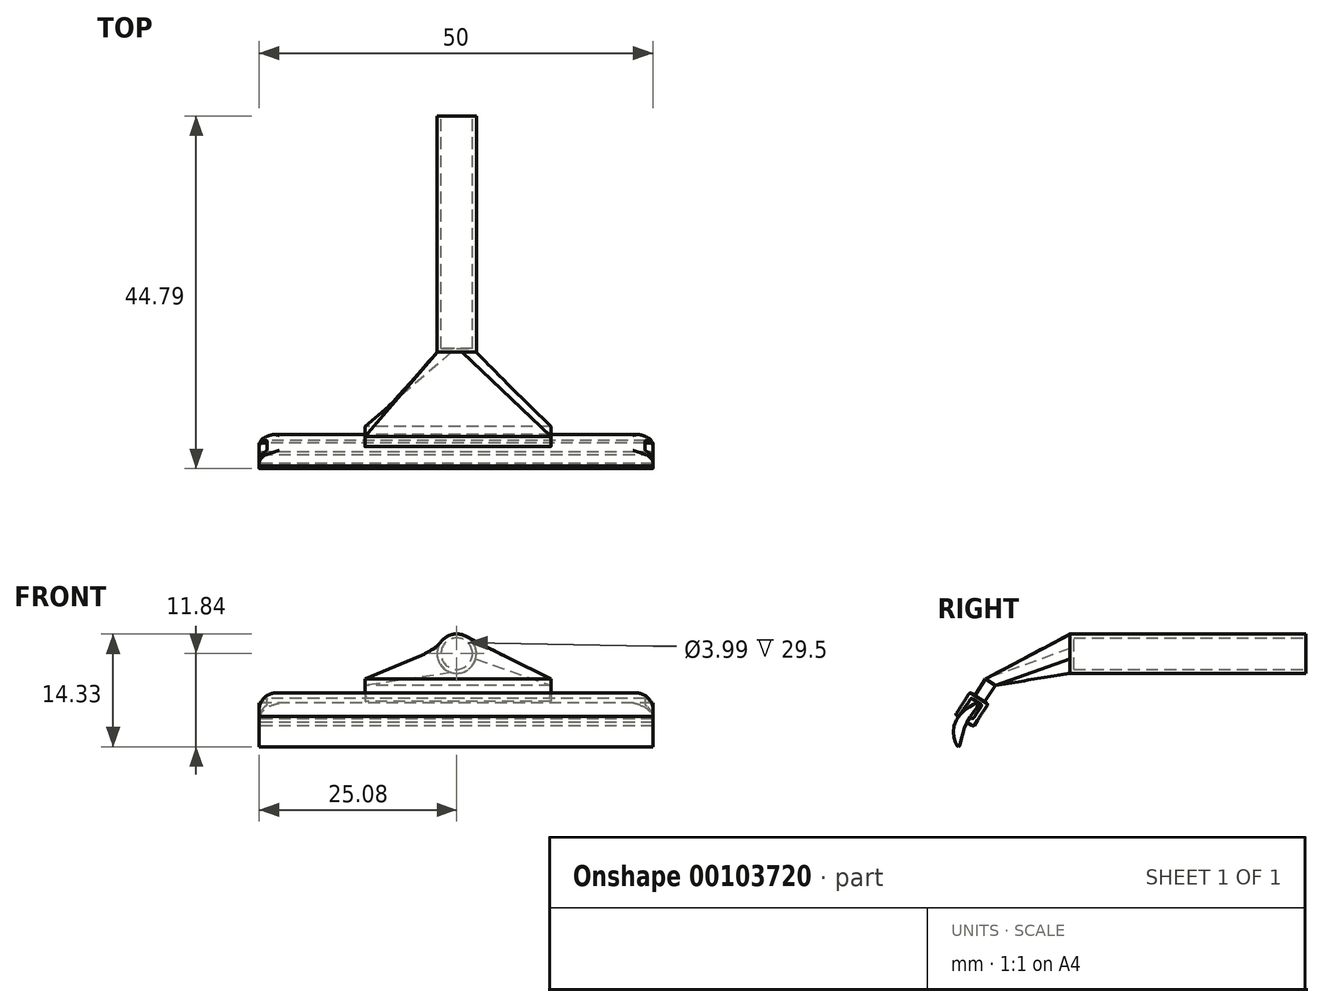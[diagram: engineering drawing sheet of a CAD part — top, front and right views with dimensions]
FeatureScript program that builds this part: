
annotation { "Feature Type Name" : "Feature", "Feature Type Description" : "" }
export const myFeature = defineFeature(function(context is Context, id is Id, definition is map)
    precondition{}
    {
        {
            var Q0;
            Q0=qCreatedBy(makeId("Right.planeOp"),FACE);
            var sketch = newSketch(context, id + "F10", { "sketchPlane" : qUnion([Q0])});
            skFitSpline(sketch, "E0", {"points": [v(-44.18, -11.84) * mm, v(-43.23, -9.04) * mm, v(-41.58, -6.28) * mm, v(-44.56, -8.68) * mm, v(-44.18, -11.84) * mm]});
            skSolve(sketch);
        }
        {
            var Q0;
            Q0=makeQuery(id+"F10.imprint","IMPRINT",FACE,{"disambiguationData":[TD([[makeQuery(id+"F10.imprint","IMPRINT",EDGE,{"derivedFrom":sQuery(id+"F10.wireOp",EDGE,"E0")}),1.0]])]});
            extrude(context, id + "F0", {"entities" : qUnion([Q0]), "depth" : 50 * mm});
        }
        {
            var Q0;
            Q0=qCreatedBy(makeId("Right.planeOp"),FACE);
            var sketch = newSketch(context, id + "F1", { "sketchPlane" : qUnion([Q0])});
            skLineSegment(sketch, "E1", {"start": v(-44.16, -8) * mm, "end": v(-44.39, -7.85) * mm});
            skLineSegment(sketch, "E2", {"start": v(-44.44, -7.6) * mm, "end": v(-42.82, -5.11) * mm});
            skLineSegment(sketch, "E3", {"start": v(-42.48, -5.04) * mm, "end": v(-40.55, -6.3) * mm});
            skLineSegment(sketch, "E4", {"start": v(-40.5, -6.57) * mm, "end": v(-42.15, -9.1) * mm});
            skLineSegment(sketch, "E5", {"start": v(-42.42, -9.15) * mm, "end": v(-43.07, -8.72) * mm});
            skLineSegment(sketch, "E6", {"start": v(-43.07, -8.72) * mm, "end": v(-42.68, -8.1) * mm});
            skLineSegment(sketch, "E7", {"start": v(-42.68, -8.1) * mm, "end": v(-42.48, -8.23) * mm});
            skLineSegment(sketch, "E8", {"start": v(-42.22, -8.18) * mm, "end": v(-41.25, -6.69) * mm});
            skLineSegment(sketch, "E9", {"start": v(-41.3, -6.43) * mm, "end": v(-42.36, -5.73) * mm});
            skLineSegment(sketch, "E10", {"start": v(-42.62, -5.78) * mm, "end": v(-44.16, -8) * mm});
            skPoint(sketch, "E11.visualSharp", {"position": v(-42.69, -4.9) * mm});
            skArc(sketch, "E11.filletArc", {"start": v(-42.48, -5.04) * mm, "mid": v(-42.67, -5) * mm, "end": v(-42.82, -5.11) * mm});
            skPoint(sketch, "E12.visualSharp", {"position": v(-40.4, -6.4) * mm});
            skArc(sketch, "E12.filletArc", {"start": v(-40.5, -6.57) * mm, "mid": v(-40.47, -6.42) * mm, "end": v(-40.55, -6.3) * mm});
            skPoint(sketch, "E13.visualSharp", {"position": v(-42.26, -9.25) * mm});
            skArc(sketch, "E13.filletArc", {"start": v(-42.42, -9.15) * mm, "mid": v(-42.27, -9.18) * mm, "end": v(-42.15, -9.1) * mm});
            skPoint(sketch, "E14.visualSharp", {"position": v(-42.33, -8.34) * mm});
            skArc(sketch, "E14.filletArc", {"start": v(-42.48, -8.23) * mm, "mid": v(-42.34, -8.26) * mm, "end": v(-42.22, -8.18) * mm});
            skPoint(sketch, "E15.visualSharp", {"position": v(-41.14, -6.53) * mm});
            skArc(sketch, "E15.filletArc", {"start": v(-41.25, -6.69) * mm, "mid": v(-41.22, -6.55) * mm, "end": v(-41.3, -6.43) * mm});
            skPoint(sketch, "E16.visualSharp", {"position": v(-42.52, -5.63) * mm});
            skArc(sketch, "E16.filletArc", {"start": v(-42.36, -5.73) * mm, "mid": v(-42.5, -5.7) * mm, "end": v(-42.62, -5.78) * mm});
            skPoint(sketch, "E17.visualSharp", {"position": v(-44.55, -7.75) * mm});
            skArc(sketch, "E17.filletArc", {"start": v(-44.44, -7.6) * mm, "mid": v(-44.47, -7.73) * mm, "end": v(-44.39, -7.85) * mm});
            skSolve(sketch);
        }
        {
            var Q0;
            Q0=makeQuery(id+"F1.imprint","IMPRINT",FACE,{"disambiguationData":[TD([[makeQuery(id+"F1.imprint","IMPRINT",EDGE,{"derivedFrom":sQuery(id+"F1.wireOp",EDGE,"E1")}),-1.0]])]});
            extrude(context, id + "F11", {"entities" : qUnion([Q0]), "depth" : 50 * mm});
        }
        {
            var Q0;
            Q0=makeQuery(id+"F11.opExtrude","SWEPT_FACE",FACE,{"disambiguationData":[OSD([sQuery(id+"F1.wireOp",EDGE,"E3")])]});
            var sketch = newSketch(context, id + "F2", { "sketchPlane" : qUnion([Q0])});
            skLineSegment(sketch, "E18.bottom", {"start": v(37.03, -32.29) * mm, "end": v(13.42, -32.29) * mm});
            skLineSegment(sketch, "E18.top", {"start": v(37.03, -30.78) * mm, "end": v(13.42, -30.78) * mm});
            skLineSegment(sketch, "E18.left", {"start": v(37.03, -32.29) * mm, "end": v(37.03, -30.78) * mm});
            skLineSegment(sketch, "E18.right", {"start": v(13.42, -32.29) * mm, "end": v(13.42, -30.78) * mm});
            skPoint(sketch, "E18.middle", {"position": v(25.23, -31.53) * mm});
            skSolve(sketch);
        }
        {
            var Q0;
            Q0 = qSketchRegion(id + "F2", true);
            extrude(context, id + "F3", {"entities" : qUnion([Q0]), "depth" : 2.5 * mm});
        }
        {
            var Q0;
            Q0=qCreatedBy(makeId("Front.planeOp"),FACE);
            var sketch = newSketch(context, id + "F4", { "sketchPlane" : qUnion([Q0])});
            skCircle(sketch, "E19", {"center": v(25.08, 0) * mm, "radius": 2.5 * mm});
            skSolve(sketch);
        }
        {
            var Q0;
            Q0=makeQuery(id+"F4.imprint","IMPRINT",FACE,{"disambiguationData":[TD([[makeQuery(id+"F4.imprint","IMPRINT",EDGE,{"derivedFrom":sQuery(id+"F4.wireOp",EDGE,"E19")}),1.0]])]});
            extrude(context, id + "F5", {"entities" : qUnion([Q0]), "depth" : 30 * mm});
        }
        {
            var Q0;
            Q0=makeQuery(id+"F5.opExtrude","CAP_FACE",FACE,{"disambiguationData":[OSD([sQuery(id+"F4.wireOp",EDGE,"E19")])],"isStart":false});
            var sketch = newSketch(context, id + "F6", { "sketchPlane" : qUnion([Q0])});
            skCircle(sketch, "E20", {"center": v(25.08, 0) * mm, "radius": 2.5 * mm});
            skPoint(sketch, "E20.first.point", {"position": v(22.59, 0) * mm});
            skPoint(sketch, "E20.second.point", {"position": v(27.57, 0) * mm});
            skPoint(sketch, "E20.third.point", {"position": v(25.22, 2.5) * mm});
            skSolve(sketch);
        }
        {
            var Q1;
            Q1 = qSketchRegion(id + "F6", true);
            var Q2;
            Q2=makeQuery(id+"F3.opExtrude","CAP_FACE",FACE,{"disambiguationData":[OSD([sQuery(id+"F2.wireOp",EDGE,"E18.bottom"),sQuery(id+"F2.wireOp",EDGE,"E18.top"),sQuery(id+"F2.wireOp",EDGE,"E18.left"),sQuery(id+"F2.wireOp",EDGE,"E18.right")])],"isStart":false});
            loft(context, id + "F7", {"sheetProfilesArray" : [{ "sheetProfileEntities" : qUnion([Q1]) }, { "sheetProfileEntities" : qUnion([Q2]) }]});
        }
        {
            var Q0;
            Q0=makeQuery(id+"F5.opExtrude","CAP_FACE",FACE,{"disambiguationData":[OSD([sQuery(id+"F4.wireOp",EDGE,"E19")])],"isStart":true});
            shell(context, id + "F8", {"entities" : qUnion([Q0]), "thickness" : 0.5 * mm});
        }
        {
            var Q0;
            Q0=makeQuery(id+"F11.opExtrude","CAP_EDGE",EDGE,{"disambiguationData":[OSD([sQuery(id+"F1.wireOp",EDGE,"E11.filletArc")])],"isStart":false});
            var Q1;
            Q1=makeQuery(id+"F11.opExtrude","CAP_EDGE",EDGE,{"disambiguationData":[OSD([sQuery(id+"F1.wireOp",EDGE,"E3")])],"isStart":false});
            var Q2;
            Q2=makeQuery(id+"F11.opExtrude","CAP_EDGE",EDGE,{"disambiguationData":[OSD([sQuery(id+"F1.wireOp",EDGE,"E12.filletArc")])],"isStart":false});
            var Q3;
            Q3=makeQuery(id+"F11.opExtrude","CAP_EDGE",EDGE,{"disambiguationData":[OSD([sQuery(id+"F1.wireOp",EDGE,"E12.filletArc")])],"isStart":true});
            var Q4;
            Q4=makeQuery(id+"F11.opExtrude","CAP_EDGE",EDGE,{"disambiguationData":[OSD([sQuery(id+"F1.wireOp",EDGE,"E3")])],"isStart":true});
            var Q5;
            Q5=makeQuery(id+"F11.opExtrude","CAP_EDGE",EDGE,{"disambiguationData":[OSD([sQuery(id+"F1.wireOp",EDGE,"E11.filletArc")])],"isStart":true});
            fillet(context, id + "F9", {"entities" : qUnion([Q0, Q1, Q2, Q3, Q4, Q5]), "radius" : 2.5 * mm, "allowEdgeOverflow" : false});
        }
        {
            var Q0;
            Q0=makeQuery(id+"F3.opExtrude","CAP_EDGE",EDGE,{"disambiguationData":[OSD([sQuery(id+"F2.wireOp",EDGE,"E18.bottom")])],"isStart":true});
            var Q1;
            Q1=makeQuery(id+"F3.opExtrude","CAP_EDGE",EDGE,{"disambiguationData":[OSD([sQuery(id+"F2.wireOp",EDGE,"E18.top")])],"isStart":true});
            var Q2;
            Q2=makeQuery(id+"F3.opExtrude","CAP_EDGE",EDGE,{"disambiguationData":[OSD([sQuery(id+"F2.wireOp",EDGE,"E18.left")])],"isStart":true});
            var Q3;
            Q3=makeQuery(id+"F3.opExtrude","CAP_EDGE",EDGE,{"disambiguationData":[OSD([sQuery(id+"F2.wireOp",EDGE,"E18.right")])],"isStart":true});
            fillet(context, id + "F12", {"entities" : qUnion([Q0, Q1, Q2, Q3]), "radius" : 0.2 * mm, "tangentPropagation" : true, "allowEdgeOverflow" : false});
        }
    });
